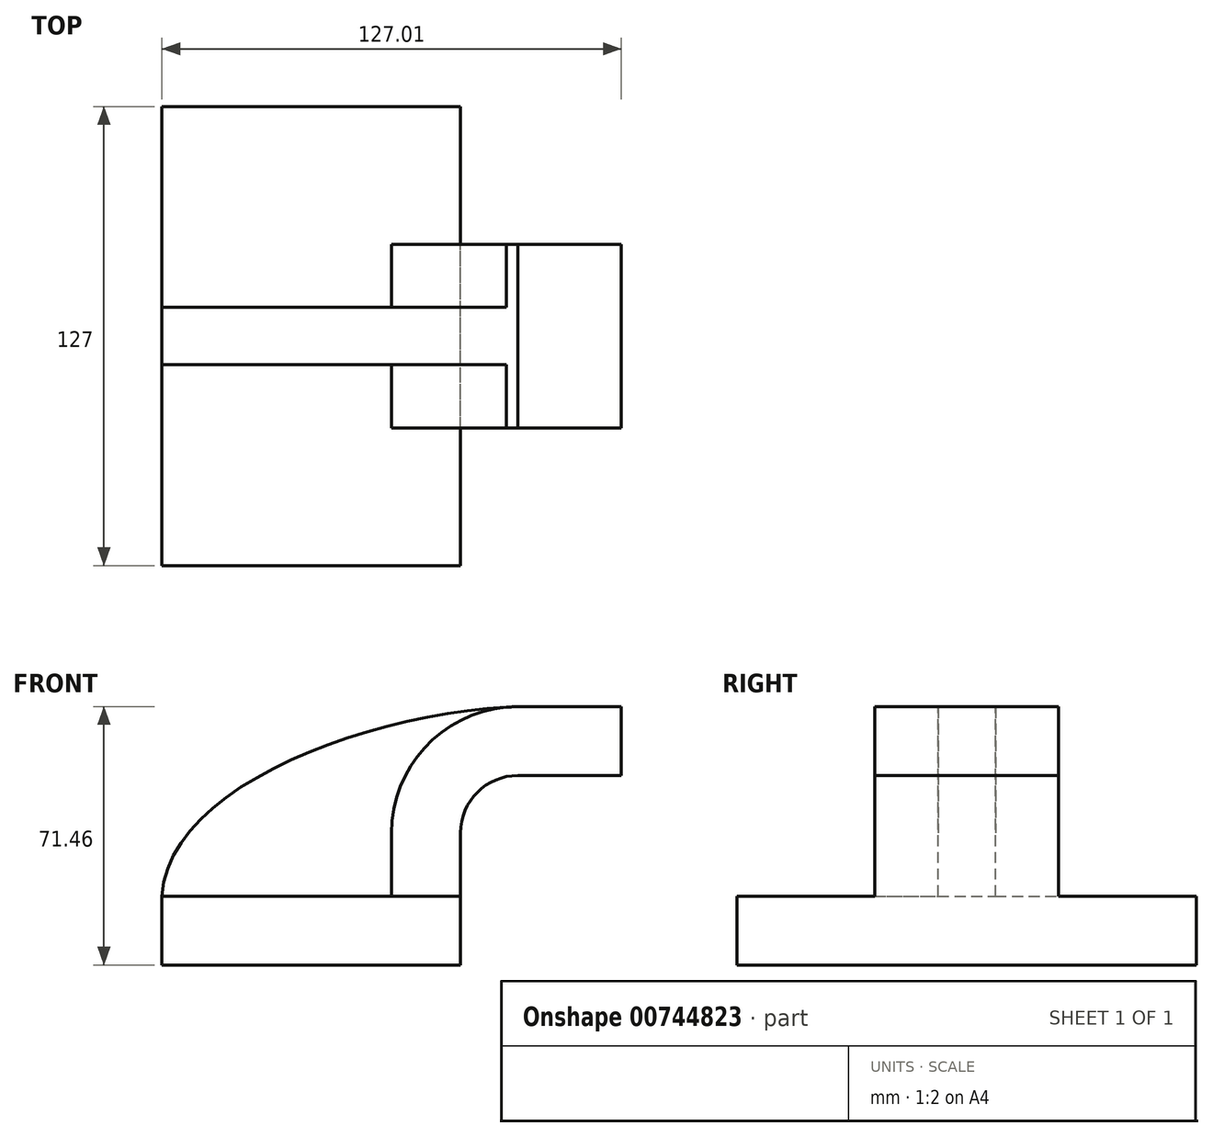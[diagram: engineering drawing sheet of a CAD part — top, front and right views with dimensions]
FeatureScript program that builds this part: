
annotation { "Feature Type Name" : "Feature", "Feature Type Description" : "" }
export const myFeature = defineFeature(function(context is Context, id is Id, definition is map)
    precondition{}
    {
        {
            var Q0;
            Q0=qCreatedBy(makeId("Front.planeOp"),FACE);
            var sketch = newSketch(context, id + "F0", { "sketchPlane" : qUnion([Q0])});
            skLineSegment(sketch, "E0.rect.bottom", {"start": v(-41.28, 9.52) * mm, "end": v(41.28, 9.52) * mm});
            skLineSegment(sketch, "E0.rect.top", {"start": v(-41.28, -9.52) * mm, "end": v(41.28, -9.52) * mm});
            skLineSegment(sketch, "E0.rect.left", {"start": v(-41.28, 9.52) * mm, "end": v(-41.28, -9.52) * mm});
            skLineSegment(sketch, "E0.rect.right", {"start": v(41.28, 9.52) * mm, "end": v(41.28, -9.52) * mm});
            skPoint(sketch, "E0.rect.middle", {"position": v(0, 0) * mm});
            skLineSegment(sketch, "E1", {"start": v(41.28, 9.52) * mm, "end": v(41.28, 27) * mm});
            skArc(sketch, "E2", {"start": v(41.28, 27) * mm, "mid": v(45.92, 38.23) * mm, "end": v(57.15, 42.88) * mm});
            skLineSegment(sketch, "E3", {"start": v(57.15, 42.88) * mm, "end": v(85.72, 42.88) * mm});
            skLineSegment(sketch, "E4.rect.bottom", {"start": v(60.32, 38.1) * mm, "end": v(111.12, 38.1) * mm});
            skLineSegment(sketch, "E4.rect.top", {"start": v(60.32, 66.68) * mm, "end": v(111.12, 66.68) * mm});
            skLineSegment(sketch, "E4.rect.left", {"start": v(60.32, 38.1) * mm, "end": v(60.32, 66.68) * mm});
            skLineSegment(sketch, "E4.rect.right", {"start": v(111.13, 38.1) * mm, "end": v(111.12, 66.68) * mm});
            skPoint(sketch, "E4.rect.middle", {"position": v(85.72, 52.39) * mm});
            skLineSegment(sketch, "E5.0", {"start": v(57.15, 61.93) * mm, "end": v(85.72, 61.93) * mm});
            skArc(sketch, "E5.1", {"start": v(22.23, 27) * mm, "mid": v(32.45, 51.7) * mm, "end": v(57.15, 61.93) * mm});
            skLineSegment(sketch, "E5.2", {"start": v(22.23, 9.52) * mm, "end": v(22.23, 27) * mm});
            skLineSegment(sketch, "E6", {"start": v(85.72, 38.1) * mm, "end": v(85.72, 66.68) * mm});
            skFitSpline(sketch, "E7", {"points": [v(-41.28, 9.53) * mm, v(57.15, 61.93) * mm], "startDerivative": vector(5.2, 92.34) * mm, "endDerivative": vector(120.92, 4.22) * mm});
            skSolve(sketch);
        }
        {
            var Q0;
            Q0=makeQuery(id+"F0.imprint","IMPRINT",FACE,{"disambiguationData":[TD([[makeQuery(id+"F0.imprint","IMPRINT",EDGE,{"derivedFrom":sQuery(id+"F0.wireOp",EDGE,"E0.rect.top")}),1.0]])]});
            extrude(context, id + "F1", {"entities" : qUnion([Q0]), "endBound" : BoundingType.SYMMETRIC, "depth" : 127 * mm});
        }
        {
            var Q0;
            {var subQ9=sQuery(id+"F0.wireOp",EDGE,"E1");Q0=makeQuery(id+"F0.imprint","IMPRINT",FACE,{"disambiguationData":[TD([[makeQuery(id+"F0.imprint","IMPRINT",EDGE,{"derivedFrom":subQ9}),1.0]])]});}
            var Q1;
            {var subQ0=sQuery(id+"F0.wireOp",EDGE,"E6");var subQ1=sQuery(id+"F0.wireOp",EDGE,"E3");var subQ2=makeQuery(id+"F0.imprint","INTERSECT",VERTEX,{"derivedFrom":[subQ1,subQ0]});Q1=makeQuery(id+"F0.imprint","IMPRINT",FACE,{"disambiguationData":[TD([[makeQuery(id+"F0.imprint","IMPRINT",EDGE,{"disambiguationData":[TD([[subQ2,1.0]])],"derivedFrom":subQ1}),1.0]])]});}
            extrude(context, id + "F2", {"entities" : qUnion([Q0, Q1]), "operationType" : NewBodyOperationType.ADD, "endBound" : BoundingType.SYMMETRIC, "depth" : 50.8 * mm});
        }
        {
            var Q0;
            {var subQ3=sQuery(id+"F0.wireOp",EDGE,"E5.2");Q0=makeQuery(id+"F0.imprint","IMPRINT",FACE,{"disambiguationData":[TD([[makeQuery(id+"F0.imprint","IMPRINT",EDGE,{"derivedFrom":subQ3}),1.0]])]});}
            extrude(context, id + "F3", {"entities" : qUnion([Q0]), "operationType" : NewBodyOperationType.ADD, "endBound" : BoundingType.SYMMETRIC, "depth" : 15.88 * mm});
        }
    });
